# Revit family: RESIDETECT
name_source: partatom
category: Luminaires
units: mm (PartAtom-declared; Revit-internal decimal feet)

## family parameters
Cote de connecteur circulaire = Utiliser le diamètre
Couper avec des vides une fois chargée = Oui
Hôte = Face
Partagée = Non
Point de calcul de pièce = Oui
Source d'éclairage = Oui
Type d'élément = Normal

## types (2) — shared parameters
Angle de l'inclinaison = 60.00°
Description = Hublot équipé dune platine LED
Détection IR/Simple
Couleur : Blanc - RAL approchant 9004
IP 44, IK 10
Diam. 304mm x Haut. 110mm
Flux restitué 948lm
Conso. système 11.6W
Efficacité lumineuse produit complet 81.7lm/W
LM80 L70F50 à 50000h (Ta25°C)
SVM 0.017
PstLM 0.052
Diffuseur Polycarbonate Direct/Symétrique Opalescent, Corps en Polycarbonate
IRC >82
Garantie 2 ans
Empreinte carbone 0.62gCO2/h
Indice de réparabilité 9,1
Elévation par défaut = 1219 mm
Emettre la visibilité des formes dans le rendu = Non
Emettre à partir du diamètre du cercle = 610 mm
Fabricant = Resistex
Filtre de couleur = 16777215
Garantie = 2 ans
Gradation des changements de température de couleur de lampe = <Aucun>
IK = IK 10
IP = IP 44
Image du type = <Aucun>
Modèle = RESIDETECT LED
Tension = 230 V
URL = https://www.resistex-sa.com
chanfrein = 2 mm  [stored 0.00656168 ft]
hauteur lum = 110 mm
indice de charge = Eclairage
nbr poles = 1
rayon = 152 mm  [stored 0.498688 ft]

## per-type parameters (varying)
| type | Charge apparente | Commentaires relatifs à la puissance | Fichier de distribution photométrique |
| 830271 | 17 VA | 11.6 | RESIDETECTLED_830271_AE.ies |
| 830251 + 931037 | 26 VA | 13 | RESIDETECT_830251_LD.ies |

note: [stored X ft] marks values corroborated as IEEE doubles in the binary element streams (Revit-internal decimal feet)
